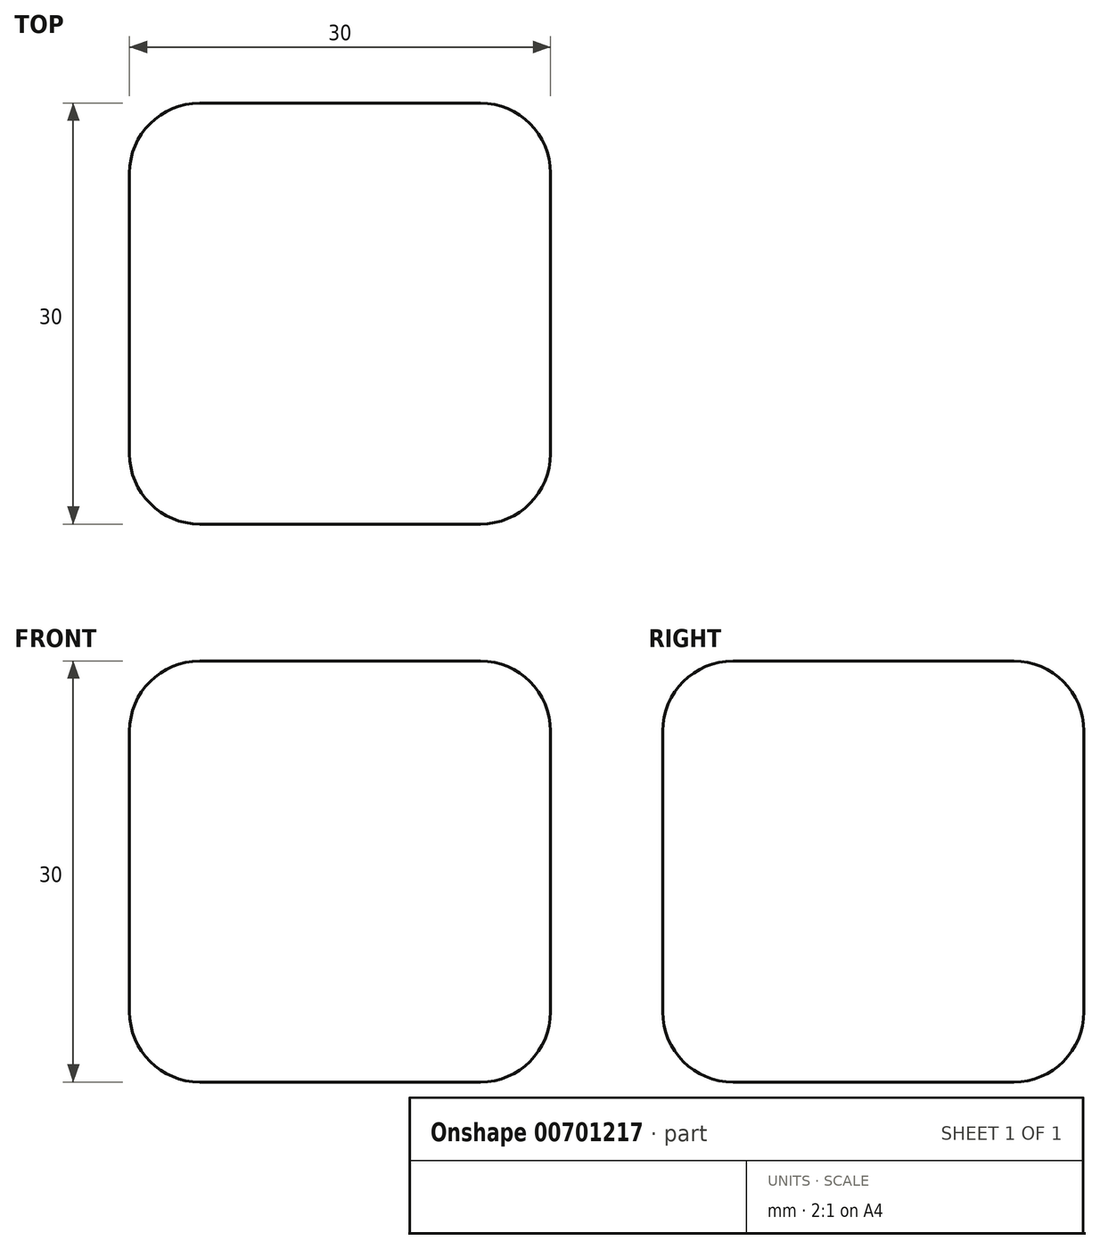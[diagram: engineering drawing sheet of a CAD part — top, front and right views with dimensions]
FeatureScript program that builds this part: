
annotation { "Feature Type Name" : "Feature", "Feature Type Description" : "" }
export const myFeature = defineFeature(function(context is Context, id is Id, definition is map)
    precondition{}
    {
        {
            var Q0;
            Q0=qCreatedBy(makeId("Front.planeOp"),FACE);
            var sketch = newSketch(context, id + "F0", { "sketchPlane" : qUnion([Q0])});
            skLineSegment(sketch, "E0.bottom", {"start": v(-7.03, 35.79) * mm, "end": v(22.97, 35.79) * mm});
            skLineSegment(sketch, "E0.top", {"start": v(-7.03, 5.79) * mm, "end": v(22.97, 5.79) * mm});
            skLineSegment(sketch, "E0.left", {"start": v(-7.03, 35.79) * mm, "end": v(-7.03, 5.79) * mm});
            skLineSegment(sketch, "E0.right", {"start": v(22.97, 35.79) * mm, "end": v(22.97, 5.79) * mm});
            skSolve(sketch);
        }
        {
            var Q0;
            Q0 = qSketchRegion(id + "F0", true);
            extrude(context, id + "F1", {"entities" : qUnion([Q0]), "depth" : 30 * mm, "offsetDistance" : 25 * mm});
        }
        {
            var Q0;
            Q0=makeQuery(id+"F1.opExtrude","CAP_EDGE",EDGE,{"disambiguationData":[OSD([sQuery(id+"F0.wireOp",EDGE,"E0.left")])],"isStart":false});
            var Q1;
            Q1=makeQuery(id+"F1.opExtrude","CAP_EDGE",EDGE,{"disambiguationData":[OSD([sQuery(id+"F0.wireOp",EDGE,"E0.right")])],"isStart":false});
            var Q2;
            Q2=makeQuery(id+"F1.opExtrude","CAP_EDGE",EDGE,{"disambiguationData":[OSD([sQuery(id+"F0.wireOp",EDGE,"E0.top")])],"isStart":false});
            var Q3;
            Q3=makeQuery(id+"F1.opExtrude","CAP_EDGE",EDGE,{"disambiguationData":[OSD([sQuery(id+"F0.wireOp",EDGE,"E0.bottom")])],"isStart":false});
            var Q4;
            Q4=makeQuery(id+"F1.opExtrude","SWEPT_EDGE",EDGE,{"disambiguationData":[OSD([sQuery(id+"F0.wireOp",EDGE,"E0.top"),sQuery(id+"F0.wireOp",EDGE,"E0.right")])]});
            var Q5;
            Q5=makeQuery(id+"F1.opExtrude","SWEPT_EDGE",EDGE,{"disambiguationData":[OSD([sQuery(id+"F0.wireOp",EDGE,"E0.top"),sQuery(id+"F0.wireOp",EDGE,"E0.left")])]});
            var Q6;
            Q6=makeQuery(id+"F1.opExtrude","SWEPT_EDGE",EDGE,{"disambiguationData":[OSD([sQuery(id+"F0.wireOp",EDGE,"E0.bottom"),sQuery(id+"F0.wireOp",EDGE,"E0.left")])]});
            var Q7;
            Q7=makeQuery(id+"F1.opExtrude","SWEPT_EDGE",EDGE,{"disambiguationData":[OSD([sQuery(id+"F0.wireOp",EDGE,"E0.bottom"),sQuery(id+"F0.wireOp",EDGE,"E0.right")])]});
            var Q8;
            Q8=makeQuery(id+"F1.opExtrude","CAP_EDGE",EDGE,{"disambiguationData":[OSD([sQuery(id+"F0.wireOp",EDGE,"E0.right")])],"isStart":true});
            var Q9;
            Q9=makeQuery(id+"F1.opExtrude","CAP_EDGE",EDGE,{"disambiguationData":[OSD([sQuery(id+"F0.wireOp",EDGE,"E0.bottom")])],"isStart":true});
            var Q10;
            Q10=makeQuery(id+"F1.opExtrude","CAP_EDGE",EDGE,{"disambiguationData":[OSD([sQuery(id+"F0.wireOp",EDGE,"E0.top")])],"isStart":true});
            var Q11;
            Q11=makeQuery(id+"F1.opExtrude","CAP_EDGE",EDGE,{"disambiguationData":[OSD([sQuery(id+"F0.wireOp",EDGE,"E0.left")])],"isStart":true});
            fillet(context, id + "F2", {"entities" : qUnion([Q0, Q1, Q2, Q3, Q4, Q5, Q6, Q7, Q8, Q9, Q10, Q11]), "radius" : 5 * mm, "tangentPropagation" : true, "allowEdgeOverflow" : false});
        }
    });
